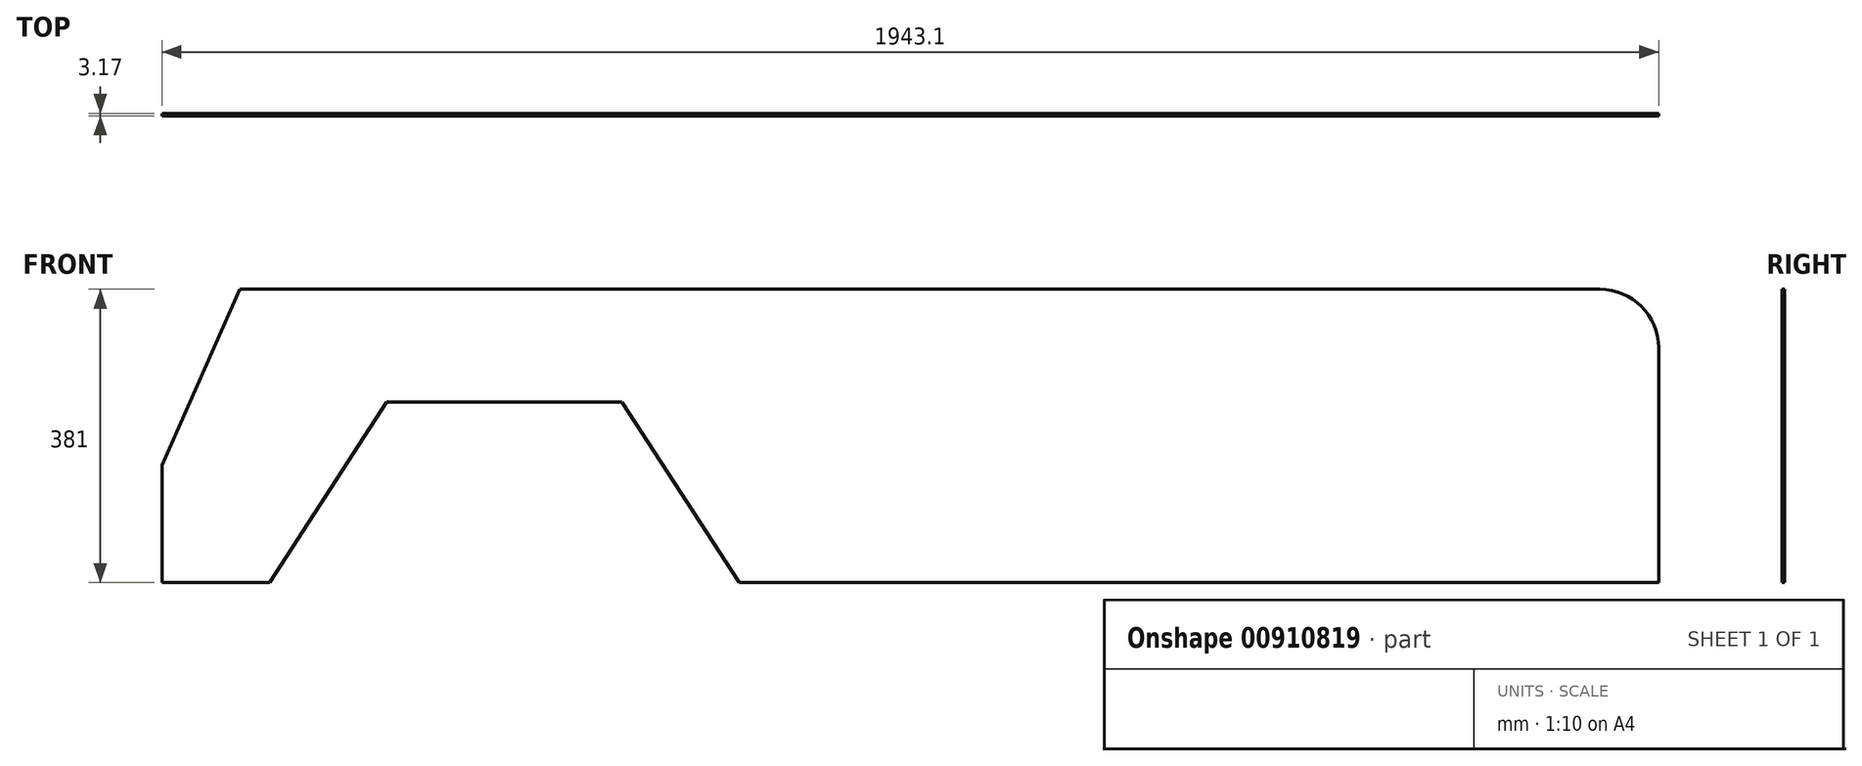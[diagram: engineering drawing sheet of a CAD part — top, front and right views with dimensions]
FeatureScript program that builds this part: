
annotation { "Feature Type Name" : "Feature", "Feature Type Description" : "" }
export const myFeature = defineFeature(function(context is Context, id is Id, definition is map)
    precondition{}
    {
        {
            var Q0;
            Q0=qCreatedBy(makeId("Front.planeOp"),FACE);
            var sketch = newSketch(context, id + "F0", { "sketchPlane" : qUnion([Q0])});
            skLineSegment(sketch, "E0.bottom", {"start": v(0, 0) * mm, "end": v(139.7, 0) * mm});
            skLineSegment(sketch, "E0.top", {"start": v(101.6, 381) * mm, "end": v(1866.9, 381) * mm});
            skLineSegment(sketch, "E0.left", {"start": v(0, 0) * mm, "end": v(0, 152.4) * mm});
            skLineSegment(sketch, "E0.right", {"start": v(1943.1, 0) * mm, "end": v(1943.1, 304.8) * mm});
            skPoint(sketch, "E1.visualSharp", {"position": v(1943.1, 381) * mm});
            skArc(sketch, "E1.filletArc", {"start": v(1943.1, 304.8) * mm, "mid": v(1920.78, 358.68) * mm, "end": v(1866.9, 381) * mm});
            skLineSegment(sketch, "E2", {"start": v(101.6, 381) * mm, "end": v(0, 152.4) * mm});
            skLineSegment(sketch, "E3", {"start": v(139.7, 0) * mm, "end": v(292.1, 234.18) * mm});
            skLineSegment(sketch, "E4", {"start": v(292.1, 234.18) * mm, "end": v(596.9, 234.18) * mm});
            skLineSegment(sketch, "E5", {"start": v(596.9, 234.18) * mm, "end": v(749.3, 0) * mm});
            skLineSegment(sketch, "E6.trimOffspring", {"start": v(749.3, 0) * mm, "end": v(1943.1, 0) * mm});
            skSolve(sketch);
        }
        {
            var Q0;
            Q0 = qSketchRegion(id + "F0", true);
            extrude(context, id + "F1", {"entities" : qUnion([Q0]), "depth" : 3.17 * mm, "offsetDistance" : 25.4 * mm});
        }
    });
